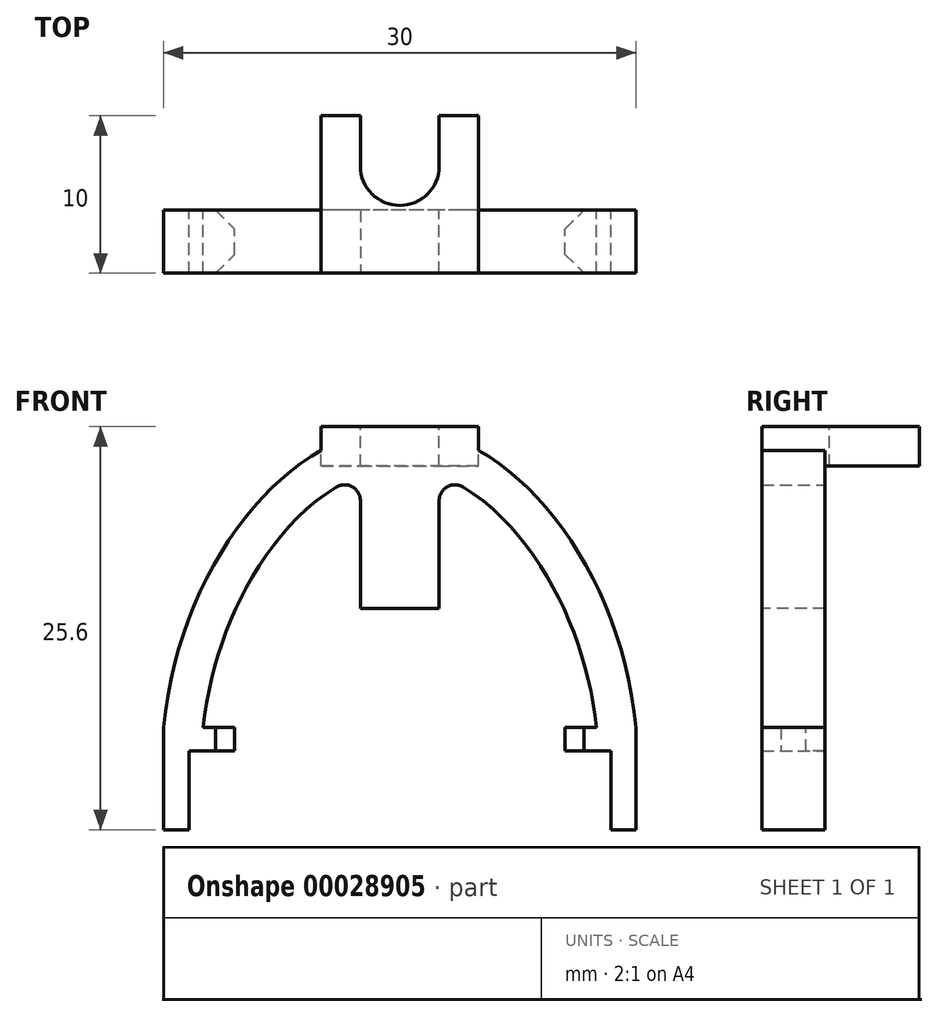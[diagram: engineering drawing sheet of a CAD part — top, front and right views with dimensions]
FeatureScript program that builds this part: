
annotation { "Feature Type Name" : "Feature", "Feature Type Description" : "" }
export const myFeature = defineFeature(function(context is Context, id is Id, definition is map)
    precondition{}
    {
        {
            var Q0;
            Q0=qCreatedBy(makeId("Front.planeOp"),FACE);
            var sketch = newSketch(context, id + "F0", { "sketchPlane" : qUnion([Q0])});
            skLineSegment(sketch, "E0", {"start": v(-15, 0) * mm, "end": v(15, 0) * mm});
            skLineSegment(sketch, "E1", {"start": v(-12.5, 9) * mm, "end": v(12.5, 9) * mm, "construction": true});
            skLineSegment(sketch, "E2", {"start": v(-30.67, 19) * mm, "end": v(34.04, 19) * mm, "construction": true});
            skFitSpline(sketch, "E3", {"points": [v(15, 0) * mm, v(0, 19) * mm, v(-15, 0) * mm], "startDerivative": vector(-6.08, 62.75) * mm, "endDerivative": vector(-6.08, -62.75) * mm});
            skSolve(sketch);
        }
        {
            var Q0;
            Q0 = qSketchRegion(id + "F0", true);
            extrude(context, id + "F1", {"entities" : qUnion([Q0]), "endBound" : BoundingType.SYMMETRIC, "depth" : 4 * mm});
        }
        {
            var Q0;
            Q0=makeQuery(id+"F1.opExtrude","CAP_FACE",FACE,{"disambiguationData":[OSD([sQuery(id+"F0.wireOp",EDGE,"E0"),sQuery(id+"F0.wireOp",EDGE,"E3")])],"isStart":false});
            var Q1;
            Q1=makeQuery(id+"F1.opExtrude","CAP_FACE",FACE,{"disambiguationData":[OSD([sQuery(id+"F0.wireOp",EDGE,"E0"),sQuery(id+"F0.wireOp",EDGE,"E3")])],"isStart":true});
            var Q2;
            Q2=makeQuery(id+"F1.opExtrude","SWEPT_FACE",FACE,{"disambiguationData":[OSD([sQuery(id+"F0.wireOp",EDGE,"E0")])]});
            shell(context, id + "F2", {"entities" : qUnion([Q0, Q1, Q2]), "thickness" : 2.5 * mm});
        }
        {
            var Q0;
            Q0=makeQuery(id+"F2.opShell","OFFSET_FACE",FACE,{"disambiguationData":[OSD([sQuery(id+"F0.wireOp",EDGE,"E0")])]});
            var sketch = newSketch(context, id + "F3", { "sketchPlane" : qUnion([Q0])});
            skLineSegment(sketch, "E4.bottom", {"start": v(-15, 2) * mm, "end": v(-10.5, 2) * mm});
            skLineSegment(sketch, "E4.top", {"start": v(-15, -2) * mm, "end": v(-10.5, -2) * mm});
            skLineSegment(sketch, "E4.left", {"start": v(-15, 2) * mm, "end": v(-15, -2) * mm});
            skLineSegment(sketch, "E4.right", {"start": v(-10.5, 2) * mm, "end": v(-10.5, -2) * mm});
            skLineSegment(sketch, "E5", {"start": v(0, 0) * mm, "end": v(0, 31.34) * mm});
            skSolve(sketch);
        }
        {
            var Q0;
            {var subQ3=sQuery(id+"F3.wireOp",EDGE,"E4.right");Q0=makeQuery(id+"F3.imprint","IMPRINT",FACE,{"disambiguationData":[TD([[makeQuery(id+"F3.imprint","IMPRINT",EDGE,{"derivedFrom":subQ3}),-1.0]])]});}
            var Q1;
            {var subQ3=sQuery(id+"F3.wireOp",EDGE,"E4.left");Q1=makeQuery(id+"F3.imprint","IMPRINT",FACE,{"disambiguationData":[TD([[makeQuery(id+"F3.imprint","IMPRINT",EDGE,{"derivedFrom":subQ3}),1.0]])]});}
            extrude(context, id + "F4", {"entities" : qUnion([Q0, Q1]), "operationType" : NewBodyOperationType.ADD, "depth" : 1.5 * mm});
        }
        {
            var Q0;
            Q0=makeQuery(id+"F1.opExtrude","SWEPT_BODY",BODY,{"disambiguationData":[OSD([sQuery(id+"F0.wireOp",EDGE,"E0"),sQuery(id+"F0.wireOp",EDGE,"E3")])]});
            var Q1;
            Q1=qCreatedBy(makeId("Right.planeOp"),FACE);
            mirror(context, id + "F5", {"operationType" : NewBodyOperationType.ADD, "entities" : qUnion([Q0]), "mirrorPlane" : qUnion([Q1])});
        }
        {
            var Q0;
            Q0=makeQuery(id+"F4.opExtrude","SWEPT_EDGE",EDGE,{"disambiguationData":[OSD([sQuery(id+"F3.wireOp",EDGE,"E4.bottom"),sQuery(id+"F3.wireOp",EDGE,"E4.right")])]});
            var Q1;
            Q1=makeQuery(id+"F4.opExtrude","SWEPT_EDGE",EDGE,{"disambiguationData":[OSD([sQuery(id+"F3.wireOp",EDGE,"E4.top"),sQuery(id+"F3.wireOp",EDGE,"E4.right")])]});
            var Q2;
            Q2=makeQuery(id+"F5.opPattern","COPY",EDGE,{"derivedFrom":makeQuery(id+"F4.opExtrude","SWEPT_EDGE",EDGE,{"disambiguationData":[OSD([sQuery(id+"F3.wireOp",EDGE,"E4.bottom"),sQuery(id+"F3.wireOp",EDGE,"E4.right")])]}),"instanceName":"1"});
            var Q3;
            Q3=makeQuery(id+"F5.opPattern","COPY",EDGE,{"derivedFrom":makeQuery(id+"F4.opExtrude","SWEPT_EDGE",EDGE,{"disambiguationData":[OSD([sQuery(id+"F3.wireOp",EDGE,"E4.top"),sQuery(id+"F3.wireOp",EDGE,"E4.right")])]}),"instanceName":"1"});
            chamfer(context, id + "F6", {"entities" : qUnion([Q0, Q1, Q2, Q3]), "width" : 1.2 * mm, "tangentPropagation" : true});
        }
        {
            var Q0;
            Q0=qCreatedBy(makeId("Top.planeOp"),FACE);
            cPlane(context, id + "F7", {"entities" : qUnion([Q0]), "cplaneType" : CPlaneType.OFFSET, "offset" : 19.1 * mm, "width" : 150 * mm, "height" : 150 * mm});
        }
        {
            var Q0;
            Q0=qCreatedBy(id+"F7.planeOp",FACE);
            var sketch = newSketch(context, id + "F8", { "sketchPlane" : qUnion([Q0])});
            skLineSegment(sketch, "E6.bottom", {"start": v(-5, -2) * mm, "end": v(5, -2) * mm});
            skLineSegment(sketch, "E6.top", {"start": v(-5, 8) * mm, "end": v(5, 8) * mm});
            skLineSegment(sketch, "E6.left", {"start": v(-5, -2) * mm, "end": v(-5, 8) * mm});
            skLineSegment(sketch, "E6.right", {"start": v(5, -2) * mm, "end": v(5, 8) * mm});
            skLineSegment(sketch, "E7", {"start": v(0, 8) * mm, "end": v(0, -2) * mm, "construction": true});
            skSolve(sketch);
        }
        {
            var Q0;
            Q0 = qSketchRegion(id + "F8", true);
            extrude(context, id + "F9", {"entities" : qUnion([Q0]), "operationType" : NewBodyOperationType.ADD, "oppositeDirection" : true, "depth" : 2.5 * mm});
        }
        {
            var Q0;
            Q0=makeQuery(id+"F9.opExtrude","CAP_FACE",FACE,{"disambiguationData":[OSD([sQuery(id+"F8.wireOp",EDGE,"E6.bottom"),sQuery(id+"F8.wireOp",EDGE,"E6.top"),sQuery(id+"F8.wireOp",EDGE,"E6.left"),sQuery(id+"F8.wireOp",EDGE,"E6.right")])],"isStart":true});
            var sketch = newSketch(context, id + "F10", { "sketchPlane" : qUnion([Q0])});
            skCircle(sketch, "E8", {"center": v(0, 4.8) * mm, "radius": 2.5 * mm});
            skLineSegment(sketch, "E9.bottom", {"start": v(-2.5, 4.8) * mm, "end": v(2.5, 4.8) * mm, "construction": true});
            skLineSegment(sketch, "E9.top", {"start": v(-2.5, 12.97) * mm, "end": v(2.5, 12.97) * mm});
            skLineSegment(sketch, "E9.left", {"start": v(-2.5, 4.8) * mm, "end": v(-2.5, 12.97) * mm});
            skLineSegment(sketch, "E9.right", {"start": v(2.5, 4.8) * mm, "end": v(2.5, 12.97) * mm});
            skSolve(sketch);
        }
        {
            var Q0;
            {var subQ5=sQuery(id+"F10.wireOp",EDGE,"E9.top");Q0=makeQuery(id+"F10.imprint","IMPRINT",FACE,{"disambiguationData":[TD([[makeQuery(id+"F10.imprint","IMPRINT",EDGE,{"derivedFrom":subQ5}),-1.0]])]});}
            var Q1;
            {var subQ0=sQuery(id+"F10.wireOp",EDGE,"E8");var subQ2=makeQuery(id+"F10.imprint","INTERSECT",VERTEX,{"derivedFrom":[subQ0,sQuery(id+"F10.wireOp",EDGE,"E9.left")]});Q1=makeQuery(id+"F10.imprint","IMPRINT",FACE,{"disambiguationData":[TD([[makeQuery(id+"F10.imprint","IMPRINT",EDGE,{"disambiguationData":[TD([[subQ2,1.0]])],"derivedFrom":subQ0}),1.0]])]});}
            var Q2;
            {var subQ3=sQuery(id+"F10.wireOp",EDGE,"E9.left");var subQ5=sQuery(id+"F10.wireOp",EDGE,"E8");var subQ7=makeQuery(id+"F10.imprint","INTERSECT",VERTEX,{"derivedFrom":[subQ5,subQ3]});Q2=makeQuery(id+"F10.imprint","IMPRINT",FACE,{"disambiguationData":[TD([[makeQuery(id+"F10.imprint","IMPRINT",EDGE,{"disambiguationData":[TD([[subQ7,1.0]])],"derivedFrom":subQ5}),-1.0]])]});}
            extrude(context, id + "F11", {"entities" : qUnion([Q0, Q1, Q2]), "operationType" : NewBodyOperationType.REMOVE, "endBound" : BoundingType.THROUGH_ALL, "oppositeDirection" : true, "depth" : 25 * mm});
        }
        {
            var Q0;
            Q0=qCreatedBy(makeId("Front.planeOp"),FACE);
            var sketch = newSketch(context, id + "F12", { "sketchPlane" : qUnion([Q0])});
            skLineSegment(sketch, "E10.bottom", {"start": v(-13.4, -1.5) * mm, "end": v(-15, -1.5) * mm});
            skLineSegment(sketch, "E10.top", {"start": v(-13.4, -6.5) * mm, "end": v(-15, -6.5) * mm});
            skLineSegment(sketch, "E10.left", {"start": v(-13.4, -1.5) * mm, "end": v(-13.4, -6.5) * mm});
            skLineSegment(sketch, "E10.right", {"start": v(-15, -1.5) * mm, "end": v(-15, -6.5) * mm});
            skLineSegment(sketch, "E11", {"start": v(0, 0) * mm, "end": v(0, -12.34) * mm, "construction": true});
            skLineSegment(sketch, "E12.MirrorCS", {"start": v(15, -1.5) * mm, "end": v(15, -6.5) * mm});
            skLineSegment(sketch, "E13.MirrorCS", {"start": v(13.4, -1.5) * mm, "end": v(13.4, -6.5) * mm});
            skLineSegment(sketch, "E14.MirrorCS", {"start": v(13.4, -1.5) * mm, "end": v(15, -1.5) * mm});
            skLineSegment(sketch, "E15.MirrorCS", {"start": v(13.4, -6.5) * mm, "end": v(15, -6.5) * mm});
            skSolve(sketch);
        }
        {
            var Q0;
            Q0 = qSketchRegion(id + "F12", true);
            extrude(context, id + "F13", {"entities" : qUnion([Q0]), "operationType" : NewBodyOperationType.ADD, "endBound" : BoundingType.SYMMETRIC, "depth" : 4 * mm});
        }
        {
            var Q0;
            {var subQ0=makeQuery(id+"F4.boolean.opBoolean","MERGE",FACE,{"derivedFrom":[makeQuery(id+"F1.opExtrude","CAP_FACE",FACE,{"disambiguationData":[OSD([sQuery(id+"F0.wireOp",EDGE,"E0"),sQuery(id+"F0.wireOp",EDGE,"E3")])],"isStart":false}),makeQuery(id+"F4.opExtrude","SWEPT_FACE",FACE,{"disambiguationData":[OSD([sQuery(id+"F3.wireOp",EDGE,"E4.bottom")])]})]});Q0=makeQuery(id+"F13.boolean.opBoolean","MERGE",FACE,{"derivedFrom":[makeQuery(id+"F9.boolean.opBoolean","MERGE",FACE,{"derivedFrom":[makeQuery(id+"F5.boolean.opBoolean","MERGE",FACE,{"derivedFrom":[subQ0,makeQuery(id+"F5.opPattern","COPY",FACE,{"derivedFrom":subQ0,"instanceName":"1"})]}),makeQuery(id+"F9.opExtrude","SWEPT_FACE",FACE,{"disambiguationData":[OSD([sQuery(id+"F8.wireOp",EDGE,"E6.bottom")])]})]}),makeQuery(id+"F13.opExtrude","CAP_FACE",FACE,{"disambiguationData":[OSD([sQuery(id+"F12.wireOp",EDGE,"E10.bottom"),sQuery(id+"F12.wireOp",EDGE,"E10.top"),sQuery(id+"F12.wireOp",EDGE,"E10.left"),sQuery(id+"F12.wireOp",EDGE,"E10.right")])],"isStart":false}),makeQuery(id+"F13.opExtrude","CAP_FACE",FACE,{"disambiguationData":[OSD([sQuery(id+"F12.wireOp",EDGE,"E12.MirrorCS"),sQuery(id+"F12.wireOp",EDGE,"E13.MirrorCS"),sQuery(id+"F12.wireOp",EDGE,"E14.MirrorCS"),sQuery(id+"F12.wireOp",EDGE,"E15.MirrorCS")])],"isStart":false})]});}
            var sketch = newSketch(context, id + "F14", { "sketchPlane" : qUnion([Q0])});
            skLineSegment(sketch, "E16.bottom", {"start": v(-2.5, 17.55) * mm, "end": v(2.5, 17.55) * mm});
            skLineSegment(sketch, "E16.top", {"start": v(-2.5, 7.55) * mm, "end": v(2.5, 7.55) * mm});
            skLineSegment(sketch, "E16.left", {"start": v(-2.5, 17.55) * mm, "end": v(-2.5, 7.55) * mm});
            skLineSegment(sketch, "E16.right", {"start": v(2.5, 17.55) * mm, "end": v(2.5, 7.55) * mm});
            skLineSegment(sketch, "E17", {"start": v(0, 17.55) * mm, "end": v(0, 7.55) * mm});
            skSolve(sketch);
        }
        {
            var Q0;
            Q0 = qSketchRegion(id + "F14", true);
            var Q1;
            {var subQ0=makeQuery(id+"F4.boolean.opBoolean","MERGE",FACE,{"derivedFrom":[makeQuery(id+"F1.opExtrude","CAP_FACE",FACE,{"disambiguationData":[OSD([sQuery(id+"F0.wireOp",EDGE,"E0"),sQuery(id+"F0.wireOp",EDGE,"E3")])],"isStart":true}),makeQuery(id+"F4.opExtrude","SWEPT_FACE",FACE,{"disambiguationData":[OSD([sQuery(id+"F3.wireOp",EDGE,"E4.top")])]})]});Q1=makeQuery(id+"F13.boolean.opBoolean","MERGE",FACE,{"derivedFrom":[makeQuery(id+"F5.boolean.opBoolean","MERGE",FACE,{"derivedFrom":[subQ0,makeQuery(id+"F5.opPattern","COPY",FACE,{"derivedFrom":subQ0,"instanceName":"1"})]}),makeQuery(id+"F13.opExtrude","CAP_FACE",FACE,{"disambiguationData":[OSD([sQuery(id+"F12.wireOp",EDGE,"E10.bottom"),sQuery(id+"F12.wireOp",EDGE,"E10.top"),sQuery(id+"F12.wireOp",EDGE,"E10.left"),sQuery(id+"F12.wireOp",EDGE,"E10.right")])],"isStart":true}),makeQuery(id+"F13.opExtrude","CAP_FACE",FACE,{"disambiguationData":[OSD([sQuery(id+"F12.wireOp",EDGE,"E12.MirrorCS"),sQuery(id+"F12.wireOp",EDGE,"E13.MirrorCS"),sQuery(id+"F12.wireOp",EDGE,"E14.MirrorCS"),sQuery(id+"F12.wireOp",EDGE,"E15.MirrorCS")])],"isStart":true})]});}
            extrude(context, id + "F15", {"entities" : qUnion([Q0]), "operationType" : NewBodyOperationType.ADD, "endBound" : BoundingType.UP_TO_SURFACE, "oppositeDirection" : true, "endBoundEntityFace" : qUnion([Q1]), "depth" : 25 * mm});
        }
        {
            var Q0;
            Q0=makeQuery(id+"F15.boolean.opBoolean","INTERSECT",EDGE,{"derivedFrom":[makeQuery(id+"F2.opShell","OFFSET_FACE",FACE,{"disambiguationData":[OSD([sQuery(id+"F0.wireOp",EDGE,"E3")])]}),makeQuery(id+"F15.opExtrude","SWEPT_FACE",FACE,{"disambiguationData":[OSD([sQuery(id+"F14.wireOp",EDGE,"E16.left")])]})]});
            var Q1;
            Q1=makeQuery(id+"F15.boolean.opBoolean","INTERSECT",EDGE,{"derivedFrom":[makeQuery(id+"F2.opShell","OFFSET_FACE",FACE,{"disambiguationData":[OSD([sQuery(id+"F0.wireOp",EDGE,"E3")])]}),makeQuery(id+"F15.opExtrude","SWEPT_FACE",FACE,{"disambiguationData":[OSD([sQuery(id+"F14.wireOp",EDGE,"E16.right")])]})]});
            fillet(context, id + "F16", {"entities" : qUnion([Q0, Q1]), "radius" : 1 * mm, "tangentPropagation" : true, "allowEdgeOverflow" : false});
        }
    });
